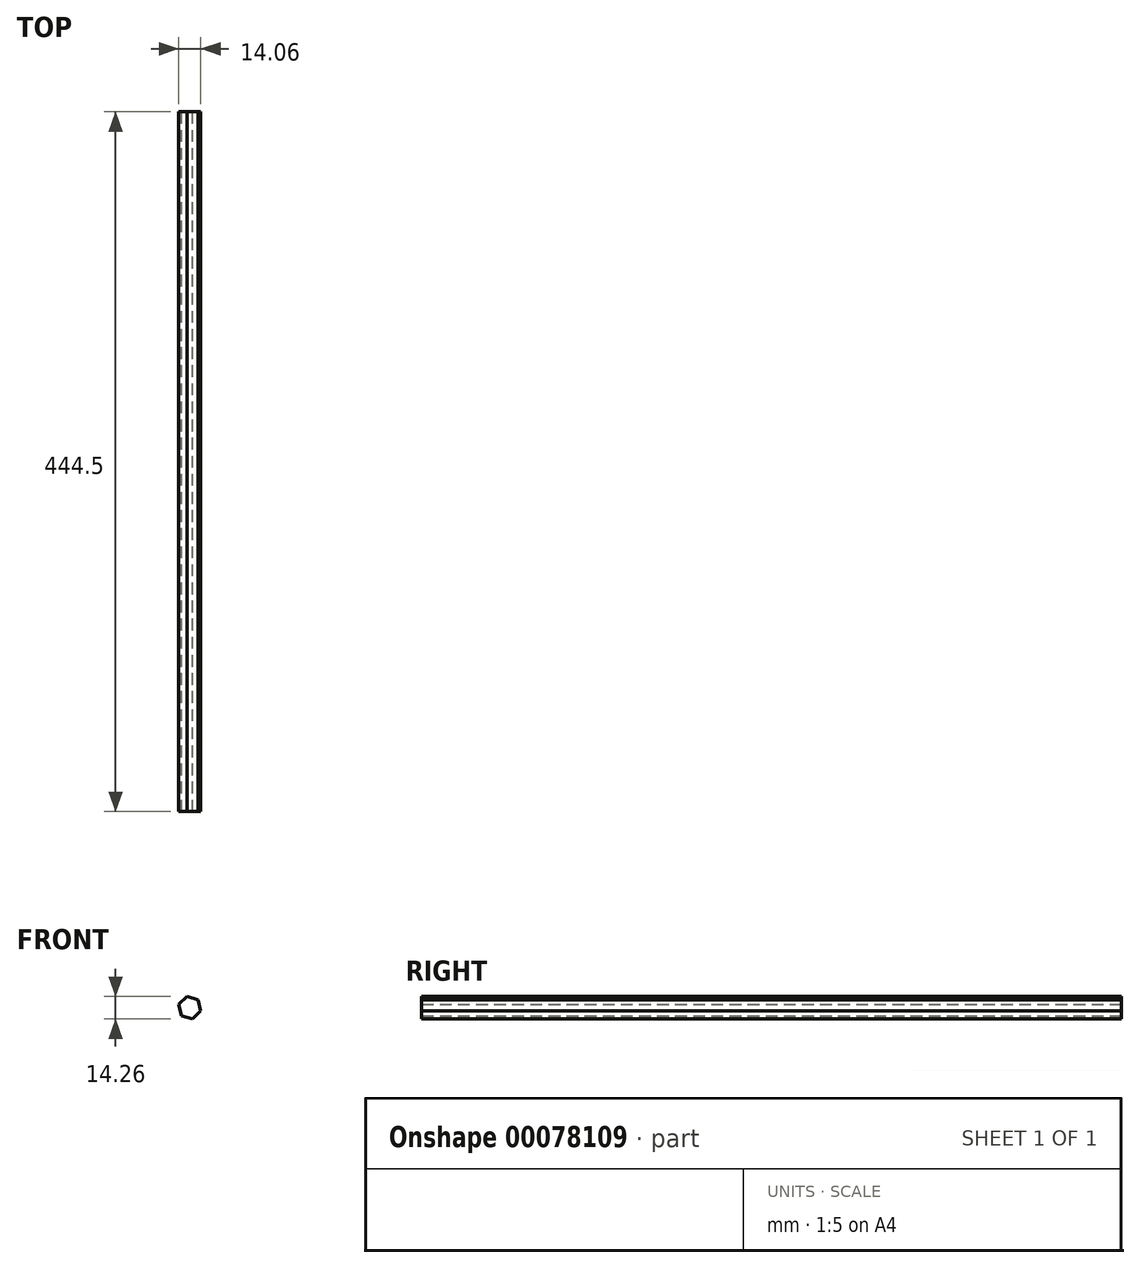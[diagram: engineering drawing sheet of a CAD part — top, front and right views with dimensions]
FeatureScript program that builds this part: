
annotation { "Feature Type Name" : "Feature", "Feature Type Description" : "" }
export const myFeature = defineFeature(function(context is Context, id is Id, definition is map)
    precondition{}
    {
        {
            var Q0;
            Q0=qCreatedBy(makeId("Front.planeOp"),FACE);
            var sketch = newSketch(context, id + "F0", { "sketchPlane" : qUnion([Q0])});
            skCircle(sketch, "E0.cCircle", {"center": v(0, 0) * mm, "radius": 7.33 * mm, "construction": true});
            skLineSegment(sketch, "E0.0", {"start": v(-1.73, 7.13) * mm, "end": v(5.3, 5.06) * mm});
            skLineSegment(sketch, "E0.1", {"start": v(5.3, 5.06) * mm, "end": v(7.03, -2.07) * mm});
            skLineSegment(sketch, "E0.2", {"start": v(7.03, -2.07) * mm, "end": v(1.73, -7.13) * mm});
            skLineSegment(sketch, "E0.3", {"start": v(1.73, -7.13) * mm, "end": v(-5.3, -5.06) * mm});
            skLineSegment(sketch, "E0.4", {"start": v(-5.3, -5.06) * mm, "end": v(-7.03, 2.07) * mm});
            skLineSegment(sketch, "E0.5", {"start": v(-7.03, 2.07) * mm, "end": v(-1.73, 7.13) * mm});
            skSolve(sketch);
        }
        {
            var Q0;
            Q0=makeQuery(id+"F0.imprint","IMPRINT",FACE,{"disambiguationData":[TD([[makeQuery(id+"F0.imprint","IMPRINT",EDGE,{"derivedFrom":sQuery(id+"F0.wireOp",EDGE,"E0.0")}),-1.0]])]});
            extrude(context, id + "F1", {"entities" : qUnion([Q0]), "depth" : 444.5 * mm});
        }
    });
